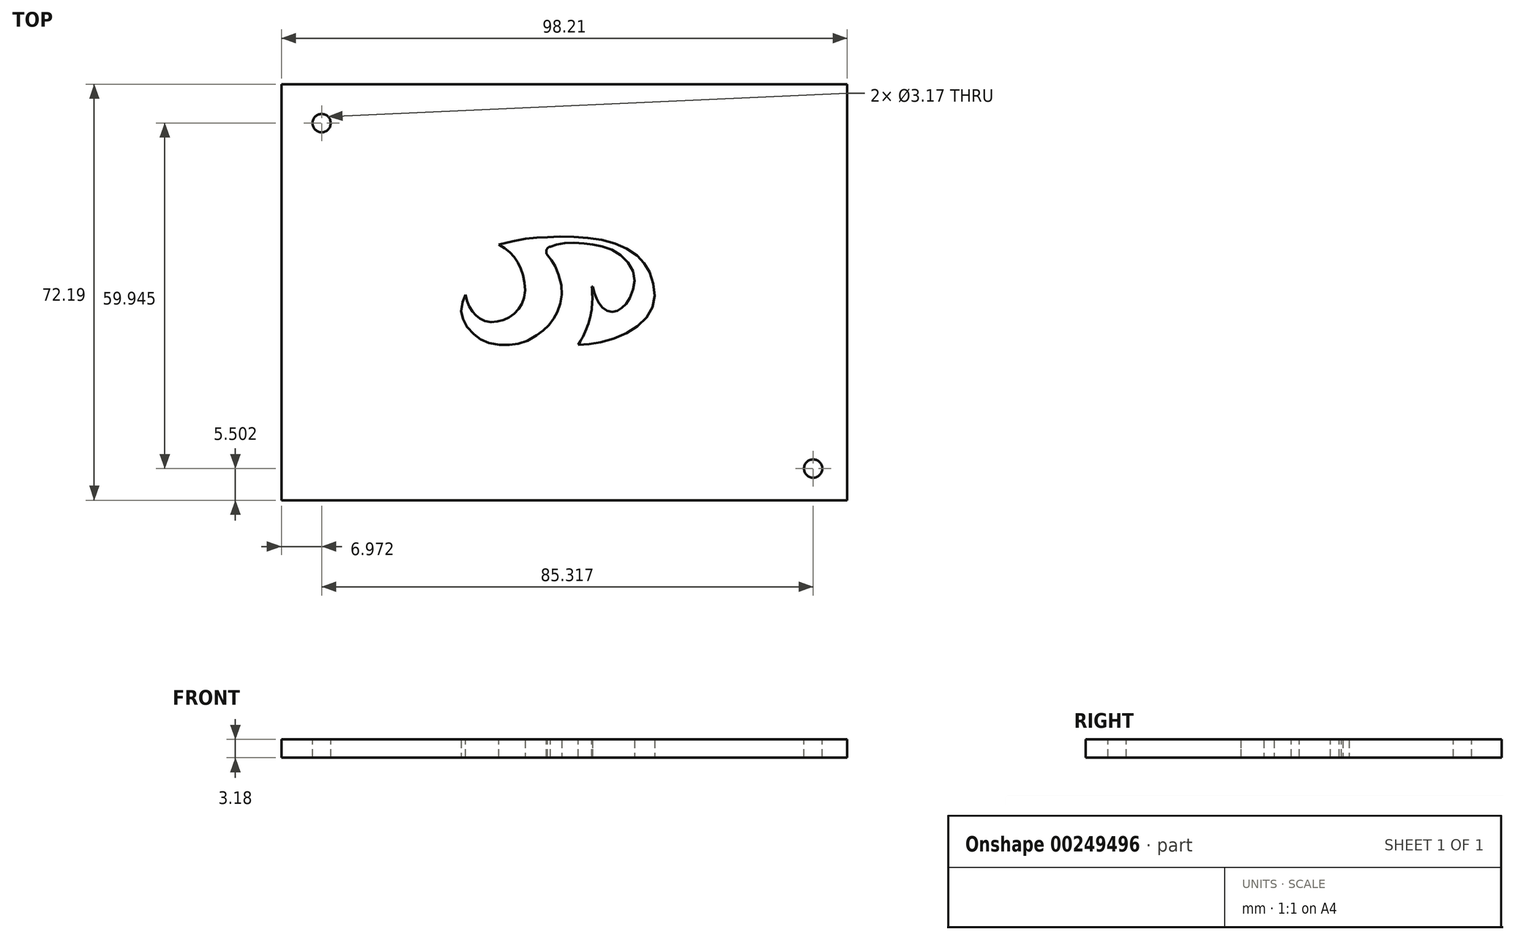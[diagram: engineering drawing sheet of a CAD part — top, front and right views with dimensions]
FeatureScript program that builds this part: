
annotation { "Feature Type Name" : "Feature", "Feature Type Description" : "" }
export const myFeature = defineFeature(function(context is Context, id is Id, definition is map)
    precondition{}
    {
        {
            var Q0;
            Q0=qCreatedBy(makeId("Top.planeOp"),FACE);
            var sketch = newSketch(context, id + "F0", { "sketchPlane" : qUnion([Q0])});
            skFitSpline(sketch, "E0", {"points": [v(-15.35, 10.6) * mm, v(-12.2, 8.85) * mm, v(-10, 6.11) * mm, v(-9.22, 2.24) * mm, v(-10.03, -0.16) * mm, v(-12.02, -1.73) * mm, v(-14.42, -2.1) * mm, v(-16.23, -1.16) * mm, v(-17.39, 0.82) * mm, v(-17.62, 2.54) * mm, v(-17.39, 4.24) * mm], "startDerivative": vector(27.97, -13.26) * mm, "endDerivative": vector(3.87, 20.92) * mm});
            skFitSpline(sketch, "E1", {"points": [v(-17.39, 4.24) * mm, v(-18.67, 3.07) * mm, v(-19.88, 0.9) * mm, v(-20.12, -2.05) * mm, v(-19.03, -4.48) * mm, v(-16.7, -6.7) * mm, v(-13.94, -7.82) * mm, v(-10.31, -7.95) * mm, v(-7.22, -7.09) * mm, v(-4.1, -4.94) * mm, v(-2.34, -2.86) * mm, v(-1.06, 0.57) * mm, v(-1.22, 4.38) * mm, v(-2.53, 7.61) * mm, v(-3.6, 9.07) * mm], "startDerivative": vector(-23.95, -19.14) * mm, "endDerivative": vector(-18.75, 21.8) * mm});
            skFitSpline(sketch, "E2", {"points": [v(-3.6, 9.07) * mm, v(-1.28, 9.6) * mm, v(3.01, 9.44) * mm, v(6.55, 8.47) * mm, v(9.1, 6.31) * mm, v(9.78, 3.67) * mm, v(8.76, 0.91) * mm, v(7.88, 0) * mm, v(6.83, -0.4) * mm, v(5.76, 0.17) * mm, v(5.22, 1.01) * mm, v(4.63, 2.57) * mm, v(4.37, 3.97) * mm], "startDerivative": vector(25.98, 7.17) * mm, "endDerivative": vector(-1.82, 13.61) * mm});
            skFitSpline(sketch, "E3", {"points": [v(4.37, 3.97) * mm, v(2.27, 3.97) * mm], "startDerivative": vector(-2.1, 0) * mm, "endDerivative": vector(-2.1, 0) * mm});
            skFitSpline(sketch, "E4", {"points": [v(2.27, 3.97) * mm, v(2.5, 1.81) * mm, v(2.15, -2.1) * mm, v(0.15, -6.6) * mm, v(-1.28, -7.95) * mm], "startDerivative": vector(1.34, -9.62) * mm, "endDerivative": vector(-6.49, -5.48) * mm});
            skFitSpline(sketch, "E5", {"points": [v(-1.28, -7.95) * mm, v(3.45, -7.8) * mm, v(9.12, -6.19) * mm, v(13.25, -3.22) * mm, v(14.95, -0.03) * mm, v(14.95, 3.6) * mm, v(13.3, 7.46) * mm, v(10.2, 10.2) * mm, v(5.55, 11.94) * mm, v(-0.44, 12.6) * mm, v(-5.5, 12.49) * mm, v(-9.49, 12.03) * mm, v(-15.35, 10.6) * mm], "startDerivative": vector(54.2, -1.2) * mm, "endDerivative": vector(-68.78, -18.83) * mm});
            skLineSegment(sketch, "E6", {"start": v(-1.28, -7.95) * mm, "end": v(-1.28, -7.95) * mm});
            skSolve(sketch);
        }
        {
            var Q0;
            Q0=qCreatedBy(makeId("Top.planeOp"),FACE);
            var sketch = newSketch(context, id + "F1", { "sketchPlane" : qUnion([Q0])});
            skLineSegment(sketch, "E7", {"start": v(0.09, -8.64) * mm, "end": v(0.1, -8.64) * mm});
            skLineSegment(sketch, "E8.bottom", {"start": v(-49.43, 38) * mm, "end": v(48.78, 38) * mm});
            skLineSegment(sketch, "E8.top", {"start": v(-49.43, -34.19) * mm, "end": v(48.78, -34.19) * mm});
            skLineSegment(sketch, "E8.left", {"start": v(-49.43, 38) * mm, "end": v(-49.43, -34.19) * mm});
            skLineSegment(sketch, "E8.right", {"start": v(48.78, 38) * mm, "end": v(48.78, -34.19) * mm});
            skCircle(sketch, "E9", {"center": v(-42.46, 31.26) * mm, "radius": 1.59 * mm});
            skCircle(sketch, "E10", {"center": v(42.86, -28.68) * mm, "radius": 1.59 * mm});
            skFitSpline(sketch, "E11.0", {"points": [v(0.07, -9.57) * mm, v(0.63, -9.59) * mm, v(1.79, -9.61) * mm, v(3.32, -9.58) * mm, v(4.61, -9.47) * mm, v(5.94, -9.3) * mm, v(7.64, -8.93) * mm, v(9.67, -8.28) * mm, v(11.6, -7.42) * mm, v(13.35, -6.35) * mm, v(14.86, -5.1) * mm, v(16.06, -3.69) * mm, v(16.9, -2.14) * mm, v(17.39, -0.48) * mm, v(17.5, 1.25) * mm, v(17.3, 3) * mm, v(16.81, 4.76) * mm, v(16.17, 6.18) * mm, v(15.5, 7.23) * mm, v(14.75, 8.2) * mm, v(13.66, 9.26) * mm, v(12.15, 10.3) * mm, v(10.48, 11.14) * mm, v(8.66, 11.8) * mm, v(6.7, 12.3) * mm, v(4.65, 12.61) * mm, v(2.56, 12.8) * mm, v(0.51, 12.87) * mm, v(-1.44, 12.86) * mm, v(-2.97, 12.8) * mm, v(-4.13, 12.74) * mm, v(-5.23, 12.66) * mm, v(-6.58, 12.53) * mm, v(-8.27, 12.28) * mm, v(-10.11, 11.9) * mm, v(-12.1, 11.4) * mm, v(-13.5, 11.02) * mm, v(-14.22, 10.83) * mm]});
            skFitSpline(sketch, "E12.0", {"points": [v(-14.38, 9.07) * mm, v(-13.8, 8.8) * mm, v(-12.94, 8.4) * mm, v(-11.93, 7.8) * mm, v(-11.25, 7.31) * mm, v(-10.65, 6.77) * mm, v(-10.12, 6.14) * mm, v(-9.67, 5.44) * mm, v(-9.3, 4.64) * mm, v(-9.01, 3.75) * mm, v(-8.83, 2.83) * mm, v(-8.77, 2.1) * mm, v(-8.78, 1.57) * mm, v(-8.82, 1.09) * mm, v(-8.95, 0.56) * mm, v(-9.2, 0.02) * mm, v(-9.54, -0.48) * mm, v(-10, -0.94) * mm, v(-10.54, -1.33) * mm, v(-11.14, -1.63) * mm, v(-11.77, -1.83) * mm, v(-12.3, -1.9) * mm, v(-12.69, -1.89) * mm, v(-13.05, -1.85) * mm, v(-13.45, -1.72) * mm, v(-13.89, -1.47) * mm, v(-14.3, -1.1) * mm, v(-14.67, -0.6) * mm, v(-14.92, -0.12) * mm, v(-15.08, 0.27) * mm, v(-15.2, 0.64) * mm, v(-15.3, 1.08) * mm, v(-15.32, 1.6) * mm, v(-15.3, 2.15) * mm, v(-15.21, 2.75) * mm, v(-15.14, 3.17) * mm, v(-15.1, 3.38) * mm]});
            skFitSpline(sketch, "E13.0", {"points": [v(-16.6, 4.29) * mm, v(-16.85, 4.09) * mm, v(-17.25, 3.77) * mm, v(-17.8, 3.23) * mm, v(-18.22, 2.76) * mm, v(-18.6, 2.22) * mm, v(-18.94, 1.63) * mm, v(-19.24, 0.98) * mm, v(-19.49, 0.27) * mm, v(-19.66, -0.46) * mm, v(-19.75, -1.21) * mm, v(-19.77, -1.97) * mm, v(-19.72, -2.72) * mm, v(-19.57, -3.45) * mm, v(-19.26, -4.36) * mm, v(-18.8, -5.2) * mm, v(-18.23, -5.98) * mm, v(-17.58, -6.74) * mm, v(-16.66, -7.6) * mm, v(-15.43, -8.47) * mm, v(-14.12, -9.09) * mm, v(-12.7, -9.47) * mm, v(-11.13, -9.65) * mm, v(-9.82, -9.65) * mm, v(-8.8, -9.57) * mm, v(-7.82, -9.44) * mm, v(-6.87, -9.2) * mm, v(-5.93, -8.85) * mm, v(-5.23, -8.52) * mm, v(-4.53, -8.12) * mm, v(-3.84, -7.69) * mm, v(-3.2, -7.22) * mm, v(-2.58, -6.74) * mm, v(-2.02, -6.26) * mm, v(-1.34, -5.62) * mm, v(-0.76, -4.95) * mm, v(-0.25, -4.18) * mm, v(0.23, -3.33) * mm, v(0.66, -2.37) * mm, v(1, -1.34) * mm, v(1.2, -0.53) * mm, v(1.33, 0.29) * mm, v(1.4, 1.38) * mm, v(1.34, 2.46) * mm, v(1.16, 3.53) * mm, v(0.9, 4.59) * mm, v(0.45, 5.86) * mm, v(-0.09, 6.97) * mm, v(-0.54, 7.72) * mm, v(-0.98, 8.37) * mm, v(-1.3, 8.76) * mm, v(-1.5, 9) * mm]});
            skArc(sketch, "E14", {"start": v(-14.21, 10.83) * mm, "mid": v(-14.9, 10) * mm, "end": v(-14.37, 9.07) * mm});
            skArc(sketch, "E15", {"start": v(-15.1, 3.38) * mm, "mid": v(-15.54, 4.36) * mm, "end": v(-16.6, 4.29) * mm});
            skFitSpline(sketch, "E16.trimOffspring", {"points": [v(-1.97, 7.48) * mm, v(-1.69, 7.56) * mm, v(-1.17, 7.71) * mm, v(-0.46, 7.9) * mm, v(0.31, 8.02) * mm, v(1.3, 8.06) * mm, v(2.43, 8.02) * mm, v(3.59, 7.92) * mm, v(4.7, 7.77) * mm, v(5.7, 7.59) * mm, v(6.6, 7.34) * mm, v(7.42, 7) * mm, v(8.2, 6.56) * mm, v(8.93, 6) * mm, v(9.52, 5.4) * mm, v(9.93, 4.76) * mm, v(10.18, 4.12) * mm, v(10.25, 3.55) * mm, v(10.22, 3.07) * mm, v(10.16, 2.68) * mm, v(10.05, 2.26) * mm, v(9.9, 1.85) * mm, v(9.74, 1.45) * mm, v(9.56, 1.1) * mm, v(9.38, 0.78) * mm, v(9.22, 0.55) * mm, v(9.08, 0.38) * mm, v(8.94, 0.24) * mm, v(8.8, 0.14) * mm, v(8.68, 0.05) * mm, v(8.56, -0.03) * mm, v(8.42, -0.11) * mm, v(8.32, -0.15) * mm, v(8.28, -0.16) * mm, v(8.26, -0.16) * mm, v(8.26, -0.16) * mm, v(8.23, -0.15) * mm, v(8.19, -0.14) * mm, v(8.1, -0.1) * mm, v(7.98, -0.02) * mm, v(7.83, 0.1) * mm, v(7.72, 0.23) * mm, v(7.63, 0.35) * mm, v(7.55, 0.48) * mm, v(7.48, 0.62) * mm, v(7.4, 0.78) * mm, v(7.3, 1.01) * mm, v(7.18, 1.3) * mm, v(7.06, 1.6) * mm, v(6.96, 1.93) * mm, v(6.84, 2.34) * mm, v(6.74, 2.9) * mm, v(6.69, 3.26) * mm, v(6.67, 3.4) * mm]});
            skLineSegment(sketch, "E17.0", {"start": v(3.64, 4.22) * mm, "end": v(5.74, 4.22) * mm});
            skArc(sketch, "E18", {"start": v(6.67, 3.4) * mm, "mid": v(6.36, 3.98) * mm, "end": v(5.74, 4.22) * mm});
            skLineSegment(sketch, "E19", {"start": v(3.64, 4.22) * mm, "end": v(5.66, -9.32) * mm});
            skSolve(sketch);
        }
        {
            var Q0;
            Q0=qCreatedBy(makeId("Top.planeOp"),FACE);
            var sketch = newSketch(context, id + "F2", { "sketchPlane" : qUnion([Q0])});
            skLineSegment(sketch, "E20", {"start": v(1.1, -10.66) * mm, "end": v(1.1, -10.66) * mm});
            skLineSegment(sketch, "E21.bottom", {"start": v(-48.43, 35.98) * mm, "end": v(49.78, 35.98) * mm});
            skLineSegment(sketch, "E21.top", {"start": v(-48.43, -36.21) * mm, "end": v(49.78, -36.21) * mm});
            skLineSegment(sketch, "E21.left", {"start": v(-48.43, 35.98) * mm, "end": v(-48.43, -36.21) * mm});
            skLineSegment(sketch, "E21.right", {"start": v(49.78, 35.98) * mm, "end": v(49.78, -36.21) * mm});
            skCircle(sketch, "E22", {"center": v(-41.46, 29.24) * mm, "radius": 1.59 * mm});
            skCircle(sketch, "E23", {"center": v(43.86, -30.7) * mm, "radius": 1.59 * mm});
            skFitSpline(sketch, "E24.0", {"points": [v(1.07, -11.6) * mm, v(1.64, -11.61) * mm, v(2.8, -11.64) * mm, v(4.33, -11.6) * mm, v(5.61, -11.5) * mm, v(6.94, -11.32) * mm, v(8.64, -10.96) * mm, v(10.67, -10.31) * mm, v(12.6, -9.45) * mm, v(14.36, -8.37) * mm, v(15.87, -7.13) * mm, v(17.07, -5.71) * mm, v(17.91, -4.17) * mm, v(18.39, -2.5) * mm, v(18.5, -0.78) * mm, v(18.3, 0.97) * mm, v(17.82, 2.74) * mm, v(17.17, 4.15) * mm, v(16.51, 5.2) * mm, v(15.76, 6.18) * mm, v(14.66, 7.23) * mm, v(13.15, 8.27) * mm, v(11.49, 9.12) * mm, v(9.67, 9.78) * mm, v(7.71, 10.26) * mm, v(5.65, 10.58) * mm, v(3.57, 10.77) * mm, v(1.52, 10.84) * mm, v(-0.43, 10.84) * mm, v(-1.97, 10.78) * mm, v(-3.12, 10.71) * mm, v(-4.23, 10.64) * mm, v(-5.58, 10.5) * mm, v(-7.26, 10.26) * mm, v(-9.1, 9.87) * mm, v(-11.1, 9.37) * mm, v(-12.5, 9) * mm, v(-13.22, 8.8) * mm]});
            skFitSpline(sketch, "E25.0", {"points": [v(-13.37, 7.05) * mm, v(-12.8, 6.77) * mm, v(-11.94, 6.37) * mm, v(-10.92, 5.77) * mm, v(-10.24, 5.29) * mm, v(-9.64, 4.74) * mm, v(-9.12, 4.12) * mm, v(-8.67, 3.42) * mm, v(-8.3, 2.62) * mm, v(-8, 1.72) * mm, v(-7.82, 0.8) * mm, v(-7.76, 0.07) * mm, v(-7.77, -0.46) * mm, v(-7.82, -0.94) * mm, v(-7.94, -1.46) * mm, v(-8.19, -2) * mm, v(-8.53, -2.5) * mm, v(-9, -2.97) * mm, v(-9.53, -3.36) * mm, v(-10.13, -3.66) * mm, v(-10.77, -3.85) * mm, v(-11.3, -3.92) * mm, v(-11.68, -3.92) * mm, v(-12.04, -3.87) * mm, v(-12.44, -3.75) * mm, v(-12.88, -3.5) * mm, v(-13.29, -3.13) * mm, v(-13.66, -2.63) * mm, v(-13.92, -2.14) * mm, v(-14.07, -1.76) * mm, v(-14.2, -1.38) * mm, v(-14.29, -0.95) * mm, v(-14.32, -0.43) * mm, v(-14.29, 0.12) * mm, v(-14.2, 0.72) * mm, v(-14.13, 1.14) * mm, v(-14.1, 1.36) * mm]});
            skFitSpline(sketch, "E26.0", {"points": [v(-15.6, 2.26) * mm, v(-15.85, 2.06) * mm, v(-16.25, 1.74) * mm, v(-16.8, 1.2) * mm, v(-17.21, 0.73) * mm, v(-17.6, 0.2) * mm, v(-17.94, -0.4) * mm, v(-18.24, -1.05) * mm, v(-18.48, -1.75) * mm, v(-18.65, -2.49) * mm, v(-18.75, -3.24) * mm, v(-18.77, -4) * mm, v(-18.71, -4.75) * mm, v(-18.57, -5.47) * mm, v(-18.26, -6.39) * mm, v(-17.8, -7.23) * mm, v(-17.22, -8) * mm, v(-16.58, -8.76) * mm, v(-15.66, -9.63) * mm, v(-14.43, -10.5) * mm, v(-13.12, -11.12) * mm, v(-11.69, -11.5) * mm, v(-10.13, -11.68) * mm, v(-8.81, -11.68) * mm, v(-7.8, -11.6) * mm, v(-6.82, -11.46) * mm, v(-5.87, -11.23) * mm, v(-4.93, -10.88) * mm, v(-4.22, -10.55) * mm, v(-3.52, -10.15) * mm, v(-2.84, -9.71) * mm, v(-2.19, -9.25) * mm, v(-1.57, -8.77) * mm, v(-1.01, -8.29) * mm, v(-0.34, -7.65) * mm, v(0.24, -6.97) * mm, v(0.76, -6.2) * mm, v(1.23, -5.36) * mm, v(1.66, -4.4) * mm, v(2, -3.36) * mm, v(2.2, -2.56) * mm, v(2.33, -1.74) * mm, v(2.4, -0.65) * mm, v(2.35, 0.43) * mm, v(2.16, 1.5) * mm, v(1.9, 2.56) * mm, v(1.45, 3.83) * mm, v(0.92, 4.94) * mm, v(0.47, 5.7) * mm, v(0.02, 6.34) * mm, v(-0.3, 6.73) * mm, v(-0.5, 6.97) * mm]});
            skArc(sketch, "E27", {"start": v(-13.2, 8.8) * mm, "mid": v(-13.9, 7.98) * mm, "end": v(-13.36, 7.04) * mm});
            skArc(sketch, "E28", {"start": v(-14.1, 1.36) * mm, "mid": v(-14.53, 2.33) * mm, "end": v(-15.6, 2.26) * mm});
            skFitSpline(sketch, "E29.trimOffspring", {"points": [v(-0.97, 5.45) * mm, v(-0.68, 5.53) * mm, v(-0.17, 5.69) * mm, v(0.55, 5.87) * mm, v(1.32, 6) * mm, v(2.31, 6.03) * mm, v(3.43, 6) * mm, v(4.59, 5.89) * mm, v(5.7, 5.74) * mm, v(6.7, 5.56) * mm, v(7.6, 5.31) * mm, v(8.42, 4.98) * mm, v(9.21, 4.53) * mm, v(9.93, 3.98) * mm, v(10.52, 3.37) * mm, v(10.94, 2.73) * mm, v(11.18, 2.1) * mm, v(11.25, 1.53) * mm, v(11.23, 1.04) * mm, v(11.16, 0.65) * mm, v(11.05, 0.24) * mm, v(10.91, -0.18) * mm, v(10.74, -0.57) * mm, v(10.57, -0.93) * mm, v(10.39, -1.24) * mm, v(10.22, -1.48) * mm, v(10.08, -1.65) * mm, v(9.94, -1.78) * mm, v(9.81, -1.89) * mm, v(9.69, -1.98) * mm, v(9.56, -2.06) * mm, v(9.42, -2.14) * mm, v(9.32, -2.17) * mm, v(9.28, -2.18) * mm, v(9.27, -2.18) * mm, v(9.27, -2.18) * mm, v(9.24, -2.18) * mm, v(9.19, -2.16) * mm, v(9.1, -2.12) * mm, v(8.98, -2.04) * mm, v(8.83, -1.92) * mm, v(8.72, -1.8) * mm, v(8.63, -1.68) * mm, v(8.56, -1.54) * mm, v(8.49, -1.4) * mm, v(8.41, -1.24) * mm, v(8.3, -1.02) * mm, v(8.18, -0.73) * mm, v(8.07, -0.42) * mm, v(7.96, -0.1) * mm, v(7.85, 0.32) * mm, v(7.74, 0.87) * mm, v(7.69, 1.24) * mm, v(7.67, 1.38) * mm]});
            skLineSegment(sketch, "E30.0", {"start": v(4.65, 2.19) * mm, "end": v(6.74, 2.19) * mm});
            skArc(sketch, "E31", {"start": v(7.67, 1.38) * mm, "mid": v(7.36, 1.96) * mm, "end": v(6.74, 2.19) * mm});
            skFitSpline(sketch, "E32.0", {"points": [v(3.72, 1.12) * mm, v(3.77, 0.72) * mm, v(3.86, 0.13) * mm, v(3.93, -0.71) * mm, v(3.97, -1.65) * mm, v(3.94, -2.7) * mm, v(3.78, -3.86) * mm, v(3.58, -4.76) * mm, v(3.3, -5.7) * mm, v(2.94, -6.64) * mm, v(2.54, -7.51) * mm, v(2.19, -8.15) * mm, v(1.9, -8.57) * mm, v(1.7, -8.83) * mm, v(1.52, -9.05) * mm, v(1.26, -9.31) * mm, v(0.93, -9.6) * mm, v(0.64, -9.82) * mm, v(0.49, -9.95) * mm]});
            skArc(sketch, "E33", {"start": v(0.58, -9.87) * mm, "mid": v(0.19, -10.92) * mm, "end": v(1.08, -11.6) * mm});
            skArc(sketch, "E34", {"start": v(4.65, 2.19) * mm, "mid": v(3.94, 1.87) * mm, "end": v(3.72, 1.12) * mm});
            skSolve(sketch);
        }
        {
            var Q0;
            Q0=makeQuery(id+"F2.imprint","IMPRINT",FACE,{"disambiguationData":[TD([[makeQuery(id+"F2.imprint","IMPRINT",EDGE,{"derivedFrom":sQuery(id+"F2.wireOp",EDGE,"E21.bottom")}),-1.0]])]});
            extrude(context, id + "F3", {"entities" : qUnion([Q0]), "oppositeDirection" : true, "depth" : 3.17 * mm});
        }
        {
            var Q0;
            Q0=qCreatedBy(makeId("Top.planeOp"),FACE);
            var sketch = newSketch(context, id + "F4", { "sketchPlane" : qUnion([Q0])});
            skLineSegment(sketch, "E35", {"start": v(0.8, -10.11) * mm, "end": v(0.8, -10.11) * mm});
            skLineSegment(sketch, "E36.bottom", {"start": v(-48.73, 36.53) * mm, "end": v(49.48, 36.53) * mm});
            skLineSegment(sketch, "E36.top", {"start": v(-48.73, -35.67) * mm, "end": v(49.48, -35.67) * mm});
            skLineSegment(sketch, "E36.left", {"start": v(-48.73, 36.53) * mm, "end": v(-48.73, -35.67) * mm});
            skLineSegment(sketch, "E36.right", {"start": v(49.48, 36.53) * mm, "end": v(49.48, -35.67) * mm});
            skCircle(sketch, "E37", {"center": v(-41.76, 29.79) * mm, "radius": 1.59 * mm});
            skCircle(sketch, "E38", {"center": v(43.56, -30.16) * mm, "radius": 1.59 * mm});
            skFitSpline(sketch, "E39.0", {"points": [v(-1.77, 7.8) * mm, v(-1.5, 7.88) * mm, v(-1, 8.03) * mm, v(-0.3, 8.22) * mm, v(0.35, 8.34) * mm, v(1.06, 8.42) * mm, v(2.02, 8.45) * mm, v(3.25, 8.41) * mm, v(4.28, 8.32) * mm, v(5.09, 8.22) * mm, v(5.87, 8.11) * mm, v(6.8, 7.94) * mm, v(7.89, 7.64) * mm, v(8.94, 7.22) * mm, v(9.95, 6.65) * mm, v(10.87, 5.94) * mm, v(11.68, 5.11) * mm, v(12.31, 4.16) * mm, v(12.72, 3.1) * mm, v(12.84, 2.16) * mm, v(12.8, 1.38) * mm, v(12.66, 0.6) * mm, v(12.37, -0.31) * mm, v(12, -1.13) * mm, v(11.68, -1.69) * mm, v(11.43, -2.05) * mm, v(11.16, -2.37) * mm, v(10.89, -2.64) * mm, v(10.64, -2.83) * mm, v(10.46, -2.97) * mm, v(10.25, -3.1) * mm, v(9.95, -3.28) * mm, v(9.59, -3.42) * mm, v(9.25, -3.5) * mm, v(8.97, -3.52) * mm, v(8.68, -3.5) * mm, v(8.42, -3.43) * mm, v(8.17, -3.35) * mm, v(7.88, -3.21) * mm, v(7.56, -3) * mm, v(7.23, -2.73) * mm, v(6.96, -2.43) * mm, v(6.74, -2.12) * mm, v(6.6, -1.87) * mm, v(6.5, -1.68) * mm, v(6.4, -1.48) * mm, v(6.29, -1.22) * mm, v(6.14, -0.88) * mm, v(6, -0.5) * mm, v(5.87, -0.1) * mm, v(5.75, 0.32) * mm, v(5.66, 0.72) * mm, v(5.57, 1.23) * mm, v(5.53, 1.53) * mm, v(5.51, 1.68) * mm]});
            skFitSpline(sketch, "E40.0", {"points": [v(5.27, 1.93) * mm, v(5.33, 1.53) * mm, v(5.42, 0.9) * mm, v(5.5, -0.04) * mm, v(5.54, -0.83) * mm, v(5.53, -1.7) * mm, v(5.46, -2.64) * mm, v(5.33, -3.64) * mm, v(5.1, -4.69) * mm, v(4.77, -5.76) * mm, v(4.37, -6.81) * mm, v(3.91, -7.8) * mm, v(3.5, -8.56) * mm, v(3.14, -9.1) * mm, v(2.77, -9.58) * mm, v(2.3, -10.08) * mm, v(1.8, -10.51) * mm, v(1.52, -10.73) * mm, v(1.4, -10.83) * mm]});
            skLineSegment(sketch, "E41.0", {"start": v(4.34, 0.86) * mm, "end": v(4.47, 0.86) * mm});
            skLineSegment(sketch, "E42.trimOffspring", {"start": v(5.41, 0.86) * mm, "end": v(5.64, 0.86) * mm});
            skFitSpline(sketch, "E43.trimOffspring", {"points": [v(5.27, 1.93) * mm, v(5.33, 1.53) * mm, v(5.42, 0.9) * mm, v(5.5, -0.04) * mm, v(5.54, -0.83) * mm, v(5.53, -1.7) * mm, v(5.46, -2.64) * mm, v(5.33, -3.64) * mm, v(5.1, -4.69) * mm, v(4.77, -5.76) * mm, v(4.37, -6.81) * mm, v(3.91, -7.8) * mm, v(3.5, -8.56) * mm, v(3.14, -9.1) * mm, v(2.77, -9.58) * mm, v(2.3, -10.08) * mm, v(1.8, -10.51) * mm, v(1.52, -10.73) * mm, v(1.4, -10.83) * mm]});
            skFitSpline(sketch, "E44.trimOffspring", {"points": [v(-14.73, 1.35) * mm, v(-14.98, 1.15) * mm, v(-15.44, 0.77) * mm, v(-16.04, 0.15) * mm, v(-16.5, -0.56) * mm, v(-16.8, -1.2) * mm, v(-17.04, -1.89) * mm, v(-17.2, -2.84) * mm, v(-17.18, -3.78) * mm, v(-17.05, -4.44) * mm, v(-16.84, -5.06) * mm, v(-16.43, -5.82) * mm, v(-15.68, -6.76) * mm, v(-14.91, -7.49) * mm, v(-14.26, -7.98) * mm, v(-13.6, -8.4) * mm, v(-12.78, -8.8) * mm, v(-11.66, -9.1) * mm, v(-10.33, -9.25) * mm, v(-9.18, -9.25) * mm, v(-8.3, -9.18) * mm, v(-7.47, -9.07) * mm, v(-6.52, -8.84) * mm, v(-5.4, -8.36) * mm, v(-4.39, -7.75) * mm, v(-3.61, -7.2) * mm, v(-3.06, -6.77) * mm, v(-2.57, -6.34) * mm, v(-2, -5.8) * mm, v(-1.55, -5.28) * mm, v(-1.15, -4.68) * mm, v(-0.85, -4.15) * mm, v(-0.57, -3.57) * mm, v(-0.23, -2.74) * mm, v(0.02, -1.85) * mm, v(0.16, -0.98) * mm, v(0.22, -0.1) * mm, v(0.16, 1) * mm, v(-0.12, 2.34) * mm, v(-0.5, 3.44) * mm, v(-0.86, 4.24) * mm, v(-1.14, 4.78) * mm, v(-1.41, 5.23) * mm, v(-1.77, 5.75) * mm, v(-2.04, 6.07) * mm, v(-2.23, 6.3) * mm]});
            skFitSpline(sketch, "E45.trimOffspring", {"points": [v(-12.87, 9.3) * mm, v(-12.29, 9.02) * mm, v(-11.39, 8.59) * mm, v(-10.22, 7.9) * mm, v(-9.37, 7.3) * mm, v(-8.6, 6.6) * mm, v(-7.9, 5.79) * mm, v(-7.32, 4.87) * mm, v(-6.84, 3.84) * mm, v(-6.5, 2.74) * mm, v(-6.2, 1.25) * mm, v(-6.16, -0.21) * mm, v(-6.45, -1.5) * mm, v(-6.85, -2.39) * mm, v(-7.4, -3.17) * mm, v(-8.07, -3.85) * mm, v(-8.86, -4.42) * mm, v(-9.73, -4.85) * mm, v(-10.66, -5.14) * mm, v(-11.62, -5.27) * mm, v(-12.58, -5.21) * mm, v(-13.5, -4.94) * mm, v(-14.17, -4.55) * mm, v(-14.66, -4.15) * mm, v(-15.1, -3.7) * mm, v(-15.56, -3.07) * mm, v(-15.99, -2.26) * mm, v(-16.29, -1.44) * mm, v(-16.5, -0.38) * mm, v(-16.49, 0.89) * mm, v(-16.32, 1.8) * mm, v(-16.24, 2.25) * mm]});
            skFitSpline(sketch, "E46.trimOffspring", {"points": [v(0.81, -9.19) * mm, v(1.38, -9.2) * mm, v(2.5, -9.23) * mm, v(3.94, -9.2) * mm, v(5.11, -9.1) * mm, v(6.31, -8.93) * mm, v(7.87, -8.6) * mm, v(9.71, -8.01) * mm, v(11.44, -7.24) * mm, v(12.98, -6.3) * mm, v(14.26, -5.23) * mm, v(15.23, -4.1) * mm, v(15.87, -2.9) * mm, v(16.24, -1.64) * mm, v(16.33, -0.28) * mm, v(16.17, 1.15) * mm, v(15.76, 2.65) * mm, v(15.22, 3.83) * mm, v(14.68, 4.68) * mm, v(14.07, 5.47) * mm, v(13.18, 6.33) * mm, v(11.9, 7.2) * mm, v(10.45, 7.95) * mm, v(8.83, 8.54) * mm, v(7.05, 8.98) * mm, v(5.13, 9.28) * mm, v(3.15, 9.45) * mm, v(1.19, 9.53) * mm, v(-0.7, 9.52) * mm, v(-2.18, 9.47) * mm, v(-3.3, 9.4) * mm, v(-4.38, 9.33) * mm, v(-5.66, 9.2) * mm, v(-7.22, 8.97) * mm, v(-8.99, 8.6) * mm, v(-10.93, 8.12) * mm, v(-12.31, 7.75) * mm, v(-13.03, 7.55) * mm]});
            skArc(sketch, "E47", {"start": v(-1.77, 7.8) * mm, "mid": v(-2.43, 7.18) * mm, "end": v(-2.23, 6.3) * mm});
            skSolve(sketch);
        }
        {
            var Q0;
            Q0=makeQuery(id+"F4.imprint","IMPRINT",FACE,{"disambiguationData":[TD([[makeQuery(id+"F4.imprint","IMPRINT",EDGE,{"derivedFrom":sQuery(id+"F4.wireOp",EDGE,"E39.0")}),1.0]])]});
            extrude(context, id + "F5", {"entities" : qUnion([Q0]), "oppositeDirection" : true, "depth" : 3.17 * mm});
        }
    });
